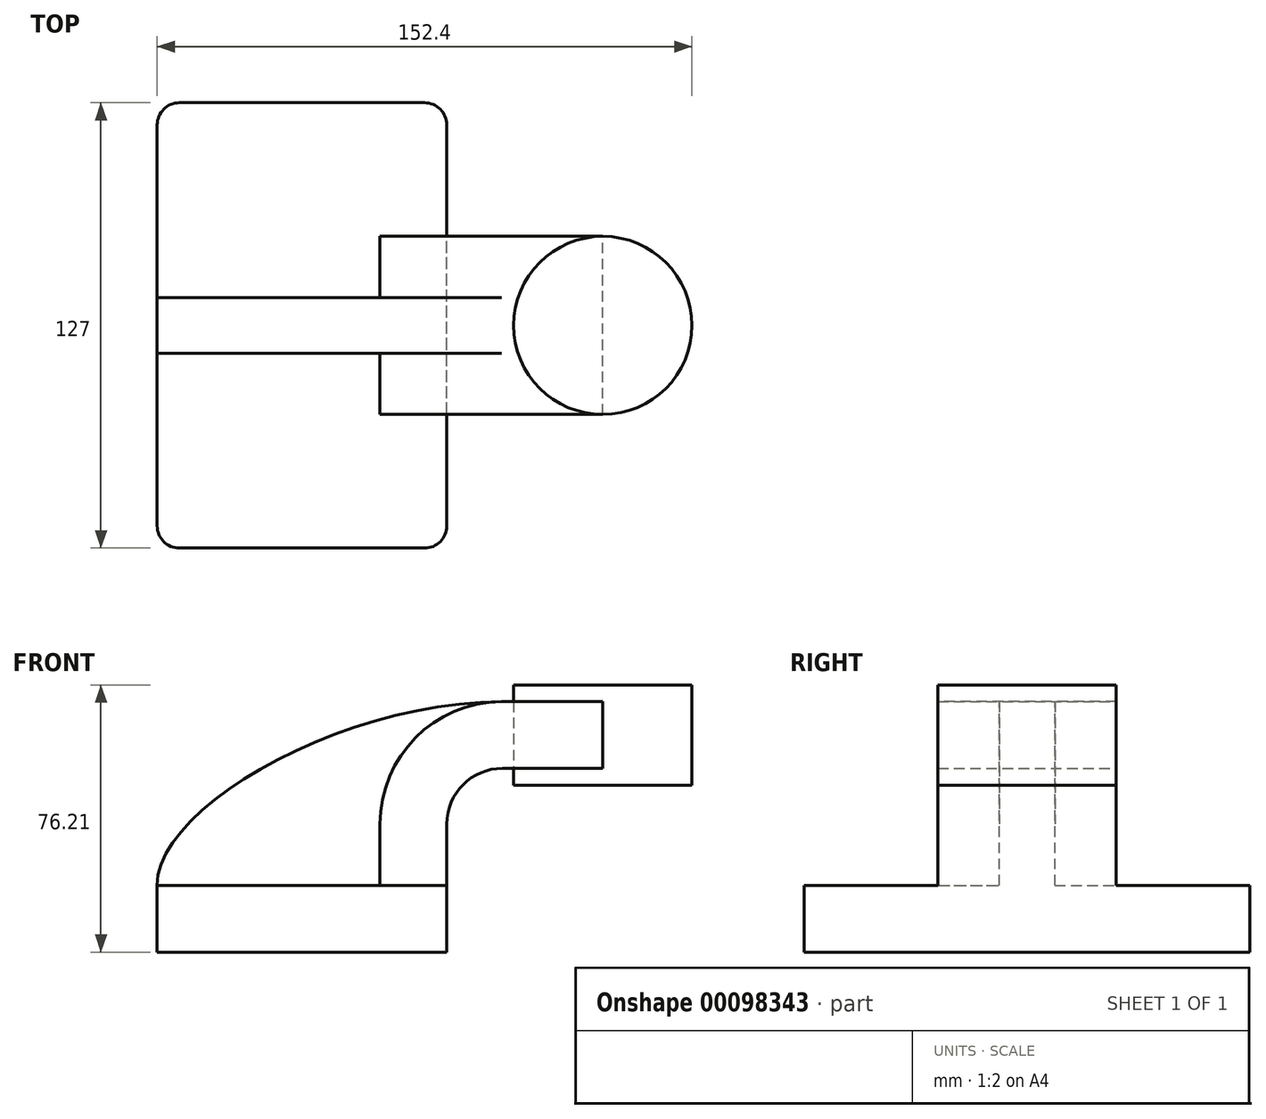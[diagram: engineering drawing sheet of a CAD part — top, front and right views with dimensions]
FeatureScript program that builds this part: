
annotation { "Feature Type Name" : "Feature", "Feature Type Description" : "" }
export const myFeature = defineFeature(function(context is Context, id is Id, definition is map)
    precondition{}
    {
        {
            var Q0;
            Q0=qCreatedBy(makeId("Front.planeOp"),FACE);
            var sketch = newSketch(context, id + "F0", { "sketchPlane" : qUnion([Q0])});
            skLineSegment(sketch, "E0.bottom", {"start": v(41.28, -9.52) * mm, "end": v(-41.28, -9.53) * mm});
            skLineSegment(sketch, "E0.top", {"start": v(41.28, 9.53) * mm, "end": v(-41.28, 9.53) * mm});
            skLineSegment(sketch, "E0.left", {"start": v(41.28, -9.52) * mm, "end": v(41.28, 9.53) * mm});
            skLineSegment(sketch, "E0.right", {"start": v(-41.28, -9.53) * mm, "end": v(-41.28, 9.53) * mm});
            skPoint(sketch, "E0.middle", {"position": v(0, 0) * mm});
            skLineSegment(sketch, "E1.bottom", {"start": v(111.12, 38.1) * mm, "end": v(60.33, 38.1) * mm});
            skLineSegment(sketch, "E1.top", {"start": v(111.12, 66.68) * mm, "end": v(60.33, 66.68) * mm});
            skLineSegment(sketch, "E1.left", {"start": v(111.12, 38.1) * mm, "end": v(111.12, 66.68) * mm});
            skLineSegment(sketch, "E1.right", {"start": v(60.33, 38.1) * mm, "end": v(60.33, 66.68) * mm});
            skPoint(sketch, "E1.middle", {"position": v(85.72, 52.39) * mm});
            skLineSegment(sketch, "E2", {"start": v(41.28, 9.53) * mm, "end": v(41.28, 27) * mm});
            skArc(sketch, "E3", {"start": v(41.27, 27) * mm, "mid": v(45.92, 38.23) * mm, "end": v(57.15, 42.88) * mm});
            skLineSegment(sketch, "E4", {"start": v(57.15, 42.88) * mm, "end": v(86.2, 42.88) * mm});
            skLineSegment(sketch, "E5.0", {"start": v(57.15, 61.93) * mm, "end": v(85.72, 61.93) * mm});
            skArc(sketch, "E5.1", {"start": v(22.23, 27) * mm, "mid": v(32.45, 51.7) * mm, "end": v(57.15, 61.93) * mm});
            skLineSegment(sketch, "E5.2", {"start": v(22.22, 9.53) * mm, "end": v(22.22, 27) * mm});
            skLineSegment(sketch, "E6", {"start": v(85.72, 38.1) * mm, "end": v(85.73, 66.68) * mm});
            skFitSpline(sketch, "E7", {"points": [v(-41.28, 9.52) * mm, v(57.15, 61.93) * mm], "startDerivative": vector(-0.36, 67.05) * mm, "endDerivative": vector(137.94, 0.34) * mm});
            skSolve(sketch);
        }
        {
            var Q0;
            Q0=makeQuery(id+"F0.imprint","IMPRINT",FACE,{"disambiguationData":[TD([[makeQuery(id+"F0.imprint","IMPRINT",EDGE,{"derivedFrom":sQuery(id+"F0.wireOp",EDGE,"E0.bottom")}),-1.0]])]});
            extrude(context, id + "F1", {"entities" : qUnion([Q0]), "endBound" : BoundingType.SYMMETRIC, "depth" : 127 * mm});
        }
        {
            var Q0;
            {var subQ1=sQuery(id+"F0.wireOp",EDGE,"E2");Q0=makeQuery(id+"F0.imprint","IMPRINT",FACE,{"disambiguationData":[TD([[makeQuery(id+"F0.imprint","IMPRINT",EDGE,{"derivedFrom":subQ1}),1.0]])]});}
            var Q1;
            {var subQ0=sQuery(id+"F0.wireOp",EDGE,"E4");var subQ1=sQuery(id+"F0.wireOp",EDGE,"E1.right");var subQ2=makeQuery(id+"F0.imprint","INTERSECT",VERTEX,{"derivedFrom":[subQ1,subQ0]});Q1=makeQuery(id+"F0.imprint","IMPRINT",FACE,{"disambiguationData":[TD([[makeQuery(id+"F0.imprint","IMPRINT",EDGE,{"disambiguationData":[TD([[subQ2,-1.0]])],"derivedFrom":subQ1}),-1.0]])]});}
            extrude(context, id + "F2", {"entities" : qUnion([Q0, Q1]), "operationType" : NewBodyOperationType.ADD, "endBound" : BoundingType.SYMMETRIC, "depth" : 50.8 * mm});
        }
        {
            var Q0;
            {var subQ3=sQuery(id+"F0.wireOp",EDGE,"E5.2");Q0=makeQuery(id+"F0.imprint","IMPRINT",FACE,{"disambiguationData":[TD([[makeQuery(id+"F0.imprint","IMPRINT",EDGE,{"derivedFrom":subQ3}),1.0]])]});}
            extrude(context, id + "F3", {"entities" : qUnion([Q0]), "operationType" : NewBodyOperationType.ADD, "endBound" : BoundingType.SYMMETRIC, "depth" : 15.88 * mm});
        }
        {
            var Q0;
            {var subQ0=sQuery(id+"F0.wireOp",EDGE,"E1.left");Q0=makeQuery(id+"F0.imprint","IMPRINT",FACE,{"disambiguationData":[TD([[makeQuery(id+"F0.imprint","IMPRINT",EDGE,{"derivedFrom":subQ0}),1.0]])]});}
            var Q1;
            Q1=sQuery(id+"F0.wireOp",EDGE,"E6");
            revolve(context, id + "F4", {"entities" : qUnion([Q0]), "axis" : qUnion([Q1]), "revolveType" : RevolveType.FULL});
        }
        {
            var Q0;
            Q0=makeQuery(id+"F1.opExtrude","CAP_EDGE",EDGE,{"disambiguationData":[OSD([sQuery(id+"F0.wireOp",EDGE,"E0.right")])],"isStart":false});
            var Q1;
            Q1=makeQuery(id+"F1.opExtrude","CAP_EDGE",EDGE,{"disambiguationData":[OSD([sQuery(id+"F0.wireOp",EDGE,"E0.left")])],"isStart":false});
            var Q2;
            Q2=makeQuery(id+"F1.opExtrude","CAP_EDGE",EDGE,{"disambiguationData":[OSD([sQuery(id+"F0.wireOp",EDGE,"E0.left")])],"isStart":true});
            var Q3;
            Q3=makeQuery(id+"F1.opExtrude","CAP_EDGE",EDGE,{"disambiguationData":[OSD([sQuery(id+"F0.wireOp",EDGE,"E0.right")])],"isStart":true});
            fillet(context, id + "F5", {"entities" : qUnion([Q0, Q1, Q2, Q3]), "radius" : 6.35 * mm, "tangentPropagation" : true, "allowEdgeOverflow" : false});
        }
    });
